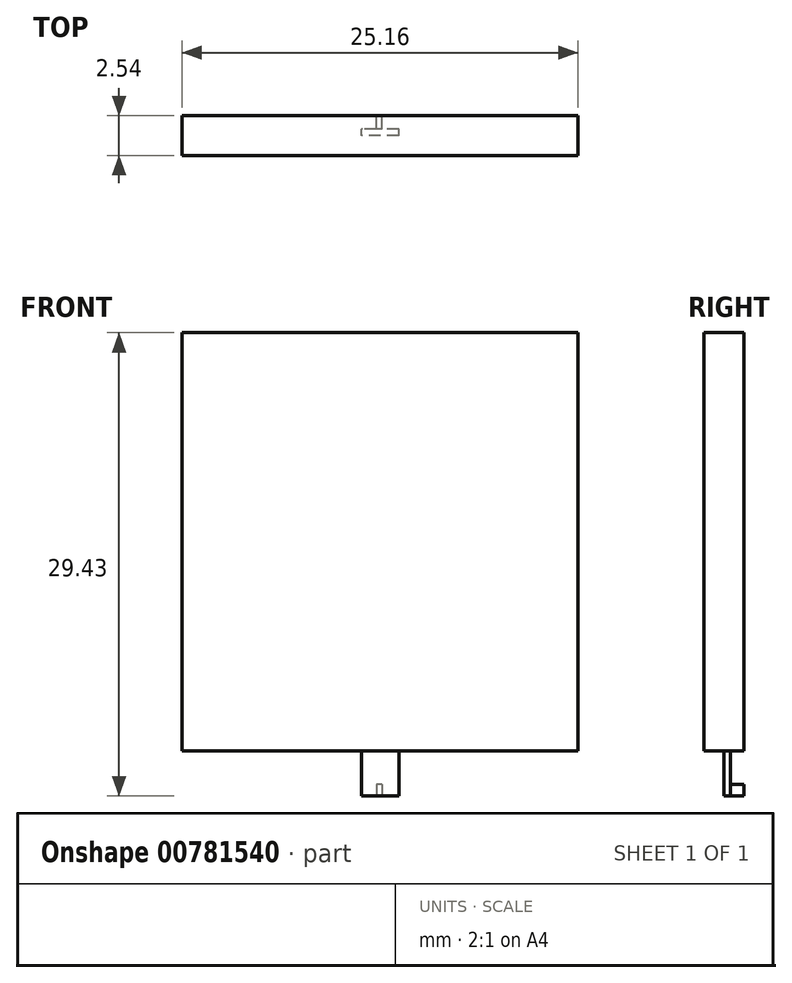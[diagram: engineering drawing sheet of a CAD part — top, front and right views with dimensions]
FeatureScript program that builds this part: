
annotation { "Feature Type Name" : "Feature", "Feature Type Description" : "" }
export const myFeature = defineFeature(function(context is Context, id is Id, definition is map)
    precondition{}
    {
        {
            var Q0;
            Q0=qCreatedBy(makeId("Front.planeOp"),FACE);
            var sketch = newSketch(context, id + "F0", { "sketchPlane" : qUnion([Q0])});
            skLineSegment(sketch, "E0.bottom", {"start": v(12.58, -13.28) * mm, "end": v(-12.58, -13.28) * mm});
            skLineSegment(sketch, "E0.top", {"start": v(12.58, 13.28) * mm, "end": v(-12.58, 13.28) * mm});
            skLineSegment(sketch, "E0.left", {"start": v(12.58, -13.28) * mm, "end": v(12.58, 13.28) * mm});
            skLineSegment(sketch, "E0.right", {"start": v(-12.58, -13.28) * mm, "end": v(-12.58, 13.28) * mm});
            skPoint(sketch, "E0.middle", {"position": v(0, 0) * mm});
            skSolve(sketch);
        }
        {
            var Q0;
            Q0 = qSketchRegion(id + "F0", true);
            extrude(context, id + "F1", {"entities" : qUnion([Q0]), "depth" : 2.54 * mm, "offsetDistance" : 25.4 * mm});
        }
        {
            var Q0;
            Q0=makeQuery(id+"F1.opExtrude","SWEPT_FACE",FACE,{"disambiguationData":[OSD([sQuery(id+"F0.wireOp",EDGE,"E0.bottom")])]});
            var sketch = newSketch(context, id + "F2", { "sketchPlane" : qUnion([Q0])});
            skLineSegment(sketch, "E1.bottom", {"start": v(1.18, 1.27) * mm, "end": v(-1.18, 1.27) * mm});
            skLineSegment(sketch, "E1.top", {"start": v(1.18, 0.86) * mm, "end": v(-1.18, 0.86) * mm});
            skLineSegment(sketch, "E1.left", {"start": v(1.18, 1.27) * mm, "end": v(1.18, 0.86) * mm});
            skLineSegment(sketch, "E1.right", {"start": v(-1.18, 1.27) * mm, "end": v(-1.18, 0.86) * mm});
            skPoint(sketch, "E1.middle", {"position": v(0, 1.06) * mm});
            skSolve(sketch);
        }
        {
            var Q0;
            Q0=makeQuery(id+"F2.imprint","IMPRINT",FACE,{"disambiguationData":[TD([[makeQuery(id+"F2.imprint","IMPRINT",EDGE,{"derivedFrom":sQuery(id+"F2.wireOp",EDGE,"E1.bottom")}),1.0]])]});
            extrude(context, id + "F3", {"entities" : qUnion([Q0]), "operationType" : NewBodyOperationType.ADD, "depth" : 2.87 * mm, "offsetDistance" : 25.4 * mm});
        }
        {
            var Q0;
            Q0=makeQuery(id+"F3.opExtrude","CAP_FACE",FACE,{"disambiguationData":[OSD([sQuery(id+"F2.wireOp",EDGE,"E1.bottom"),sQuery(id+"F2.wireOp",EDGE,"E1.top"),sQuery(id+"F2.wireOp",EDGE,"E1.left"),sQuery(id+"F2.wireOp",EDGE,"E1.right")])],"isStart":false});
            var sketch = newSketch(context, id + "F4", { "sketchPlane" : qUnion([Q0])});
            skLineSegment(sketch, "E2.bottom", {"start": v(-0.23, 0.86) * mm, "end": v(0.13, 0.86) * mm});
            skLineSegment(sketch, "E2.top", {"start": v(-0.23, 0) * mm, "end": v(0.13, 0) * mm});
            skLineSegment(sketch, "E2.left", {"start": v(-0.23, 0.86) * mm, "end": v(-0.23, 0) * mm});
            skLineSegment(sketch, "E2.right", {"start": v(0.13, 0.86) * mm, "end": v(0.13, 0) * mm});
            skSolve(sketch);
        }
        {
            var Q0;
            Q0=makeQuery(id+"F4.imprint","IMPRINT",FACE,{"disambiguationData":[TD([[makeQuery(id+"F4.imprint","IMPRINT",EDGE,{"derivedFrom":sQuery(id+"F4.wireOp",EDGE,"E2.bottom")}),1.0]])]});
            extrude(context, id + "F5", {"entities" : qUnion([Q0]), "operationType" : NewBodyOperationType.ADD, "oppositeDirection" : true, "depth" : 0.74 * mm, "offsetDistance" : 25.4 * mm});
        }
    });
